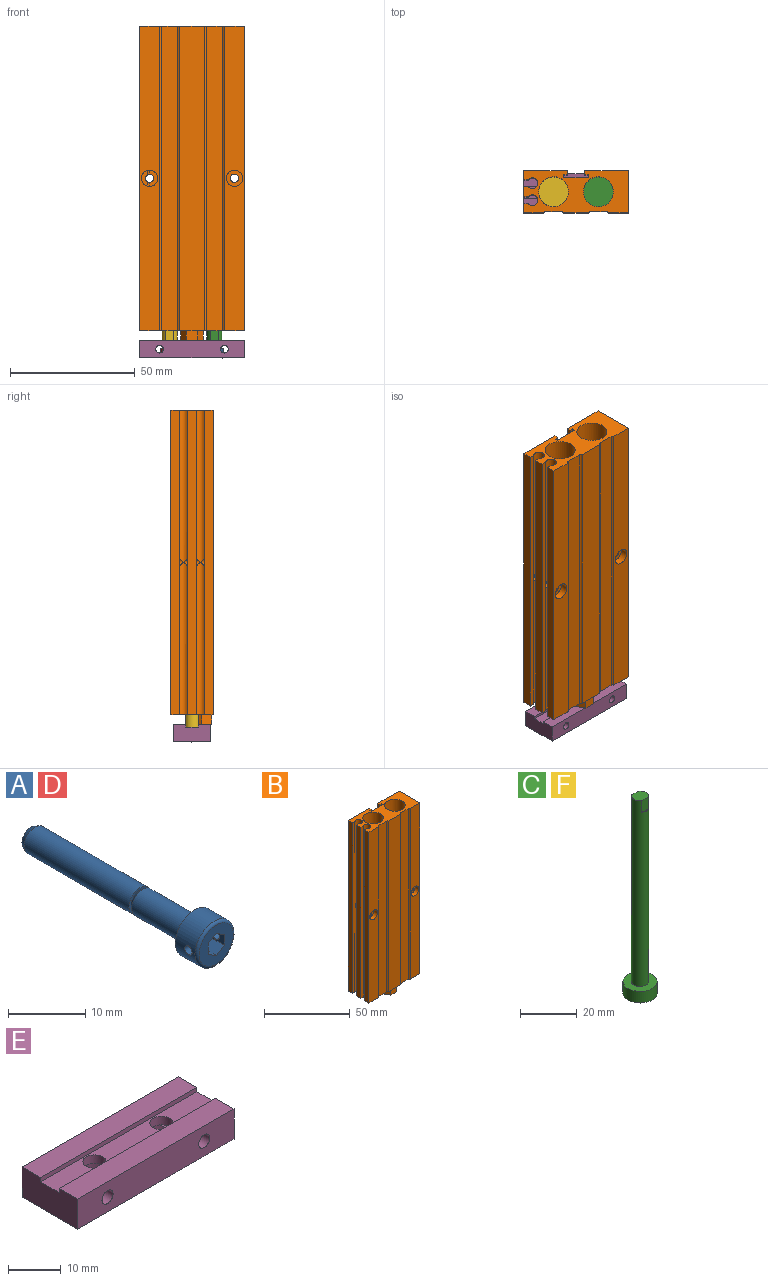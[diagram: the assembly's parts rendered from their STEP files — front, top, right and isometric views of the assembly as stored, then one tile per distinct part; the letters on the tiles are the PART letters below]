
ASSEMBLY  parts=6 mates=11
PART A: 19 faces, bbox 7.6x34x7.6 mm
  f0: cylinder r=3.5mm len=7mm, axis (0,1,0), area 76.8mm2, adj f1,f7,f8,f18
  f1: torus R=3.1mm, axis (0,1,0), area 13.2mm2, adj f0,f17
  f2: cone r=1.81mm half-angle=26.6deg, axis (0,-1,0), area 9.6mm2, adj f3,f16
  f3: cylinder r=2mm len=19.24mm, axis (0,1,0), area 241.8mm2, adj f2,f15
  f4: cone r=1.81mm half-angle=37.2deg, axis (0,-1,0), area 7.1mm2, adj f5,f15
  f5: cylinder r=2mm len=9.5mm, axis (0,1,0), area 119.4mm2, adj f4,f18
  f6: cone r=1.15mm half-angle=60deg, axis (0,-1,0), area 9mm2, adj f9,f10,f11,f12,f13,f14
  f7: cylinder r=0.68mm len=2mm, axis (-1,0,0), area 8.4mm2, adj f0,f9
  f8: cylinder r=0.68mm len=2mm, axis (1,0,0), area 8.4mm2, adj f0,f12
  f9: plane 2.52x1.86mm, normal (1,0,0), area 2.7mm2, adj f6,f7,f10,f14,f17
  f10: plane 2.52x1.63mm, normal (0.5,0,0.87), area 4.2mm2, adj f6,f9,f11,f17
  f11: plane 2.52x1.63mm, normal (-0.5,0,0.87), area 4.2mm2, adj f6,f10,f12,f17
  f12: plane 2.52x1.86mm, normal (-1,0,0), area 2.7mm2, adj f6,f8,f11,f13,f17
  f13: plane 2.52x1.63mm, normal (-0.5,0,-0.87), area 4.2mm2, adj f6,f12,f14,f17
  f14: plane 2.52x1.63mm, normal (0.5,0,-0.87), area 4.2mm2, adj f6,f9,f13,f17
  f15: plane 4x4mm, normal (0,-1,0), area 4.3mm2, adj f3,f4
  f16: plane 3.24x3.24mm, normal (0,1,0), area 8.3mm2, adj f2
  f17: plane 6.2x6.2mm, normal (0,-1,0), area 22.4mm2, adj f1,f9,f10,f11,f12,f13,f14
  f18: plane 7x7mm, normal (0,1,0), area 25.9mm2, adj f0,f5
PART B: 53 faces, bbox 42x17x126 mm
  f0: cylinder r=2.15mm len=122mm, axis (0,0,1), area 1219.4mm2, adj f6,f7,f15,f16,f37,f39,f40,f41
  f1: cylinder r=2.15mm len=122mm, axis (0,0,1), area 1222.4mm2, adj f6,f7,f17,f18,f37,f38
  f2: plane 122x17mm, normal (1,0,0), area 2012.3mm2, adj f6,f7,f11,f13,f32,f33
  f3: cylinder r=6mm len=126mm, axis (0,0,1), area 4544.2mm2, adj f6,f7,f32,f33,f44,f51,f52
  f4: plane 122x7.99mm, normal (0,-1,0), area 941.1mm2, adj f6,f7,f12,f30,f43
  f5: plane 122x9.97mm, normal (0,-1,0), area 1216.5mm2, adj f6,f7,f26,f31
  f6: plane 42x17mm, normal (0,0,1), area 414.9mm2, adj f0,f1,f2,f3,f4,f5,f8,f9
  f7: plane 42x17mm, normal (0,0,-1), area 362.5mm2, adj f0,f1,f2,f3,f4,f5,f8,f9
  f8: plane 122x17.5mm, normal (0,1,0), area 2126.4mm2, adj f6,f7,f9,f21,f38
  f9: plane 122x3.6mm, normal (-1,0,0), area 439.2mm2, adj f6,f7,f8,f17
  f10: plane 122x3.8mm, normal (-1,0,0), area 463.6mm2, adj f6,f7,f16,f18
  f11: plane 122x17.5mm, normal (0,1,0), area 2126.4mm2, adj f2,f6,f7,f20,f34
  f12: plane 122x3.6mm, normal (-1,0,0), area 439.2mm2, adj f4,f6,f7,f15
  f13: plane 122x7.99mm, normal (0,-1,0), area 941.1mm2, adj f2,f6,f7,f27,f36
  f14: cylinder r=6mm len=126mm, axis (0,0,1), area 4608.3mm2, adj f6,f7,f48,f49,f52
  f15: plane 122x1.96mm, normal (0,1,0), area 239.1mm2, adj f0,f6,f7,f12
  f16: plane 122x1.96mm, normal (0,-1,0), area 239.1mm2, adj f0,f6,f7,f10
  f17: plane 122x1.96mm, normal (0,-1,0), area 239.1mm2, adj f1,f6,f7,f9
  f18: plane 122x1.96mm, normal (0,1,0), area 239.1mm2, adj f1,f6,f7,f10
  f19: plane 122x1.5mm, normal (0,-1,0), area 183mm2, adj f6,f7,f20,f25
  f20: plane 122x1.62mm, normal (-1,0,0), area 197.6mm2, adj f6,f7,f11,f19
  f21: plane 122x1.62mm, normal (1,0,0), area 197.6mm2, adj f6,f7,f8,f22
  f22: plane 122x1.5mm, normal (0,-1,0), area 183mm2, adj f6,f7,f21,f23
  f23: plane 122x1.28mm, normal (1,0,0), area 156.2mm2, adj f6,f7,f22,f24
  f24: plane 122x10mm, normal (0,1,0), area 1220mm2, adj f6,f7,f23,f25
  f25: plane 122x1.28mm, normal (-1,0,0), area 156.2mm2, adj f6,f7,f19,f24
  f26: cylinder r=1mm len=122mm, axis (0,0,1), area 154.5mm2, adj f5,f6,f7,f28
  f27: cylinder r=1mm len=122mm, axis (0,0,1), area 154.5mm2, adj f6,f7,f13,f28
  f28: plane 122x6.12mm, normal (0,-1,0), area 746.7mm2, adj f6,f7,f26,f27
  f29: plane 122x6.12mm, normal (0,-1,0), area 746.7mm2, adj f6,f7,f30,f31
  f30: cylinder r=1mm len=122mm, axis (0,0,1), area 154.5mm2, adj f4,f6,f7,f29
  f31: cylinder r=1mm len=122mm, axis (0,0,1), area 154.5mm2, adj f5,f6,f7,f29
  f32: cylinder r=3.13mm len=6.88mm, axis (1,0,0), area 126.7mm2, adj f2,f3
  f33: cylinder r=3.13mm len=6.88mm, axis (1,0,0), area 126.7mm2, adj f2,f3
  f34: cylinder r=1.65mm len=14mm, axis (0,-1,0), area 145.1mm2, adj f11,f35
  f35: plane 6.5x6.5mm, normal (0,-1,0), area 24.6mm2, adj f34,f36
  f36: cylinder r=3.25mm len=6.5mm, axis (0,-1,0), area 61.3mm2, adj f13,f35
  f37: cylinder r=1.65mm len=6.45mm, axis (0,-1,0), area 36.5mm2, adj f0,f1
  f38: cylinder r=1.65mm len=4.93mm, axis (0,-1,0), area 35.9mm2, adj f1,f8
  f39: plane 6.5x3.28mm, normal (0,-1,0), area 12.4mm2, adj f0,f40,f43
  f40: cylinder r=1.65mm len=3.3mm, axis (0,-1,0), area 4.3mm2, adj f0,f39
  f41: cylinder r=1.65mm len=2.69mm, axis (0,-1,0), area 0.5mm2, adj f0,f42
  f42: plane 6.21x2.3mm, normal (0,-1,0), area 9.2mm2, adj f0,f41,f43
  f43: cylinder r=3.25mm len=6.5mm, axis (0,-1,0), area 61.3mm2, adj f0,f4,f39,f42
  f44: plane 4x0.08mm, normal (0.87,0.5,0), area 0.4mm2, adj f3,f7,f45,f52
  f45: plane 4x3.9mm, normal (0.87,-0.5,0), area 18mm2, adj f7,f44,f46,f52
  f46: plane 4.5x4mm, normal (0,-1,0), area 18mm2, adj f7,f45,f47,f52
  f47: plane 4x3.9mm, normal (-0.87,-0.5,0), area 18mm2, adj f7,f46,f48,f52
  f48: plane 4x0.08mm, normal (-0.87,0.5,0), area 0.4mm2, adj f7,f14,f47,f52
  f49: plane 4x1.88mm, normal (-0.87,0.5,0), area 8.7mm2, adj f7,f14,f50,f52
  f50: plane 4.5x4mm, normal (0,1,0), area 18mm2, adj f7,f49,f51,f52
  f51: plane 4x1.88mm, normal (0.87,0.5,0), area 8.7mm2, adj f3,f7,f50,f52
  f52: plane 9.01x7.8mm, normal (0,0,-1), area 52.4mm2, adj f3,f14,f44,f45,f46,f47,f48,f49
PART C: 9 faces, bbox 12x12x85 mm
  f0: cylinder r=3mm len=80mm, axis (0,0,-1), area 1472.8mm2, adj f1,f4,f5,f6,f7,f8
  f1: plane 6x5mm, normal (0,0,1), area 26mm2, adj f0,f5,f8
  f2: cylinder r=6mm len=12mm, axis (0,0,1), area 188.5mm2, adj f3,f4
  f3: plane 12x12mm, normal (0,0,-1), area 113.1mm2, adj f2
  f4: plane 12x12mm, normal (0,0,1), area 84.8mm2, adj f0,f2
  f5: plane 5x3.32mm, normal (0,-1,0), area 16.6mm2, adj f0,f1,f6
  f6: plane 3.32x0.5mm, normal (0,0,1), area 1.1mm2, adj f0,f5
  f7: plane 3.32x0.5mm, normal (0,0,1), area 1.1mm2, adj f0,f8
  f8: plane 5x3.32mm, normal (0,1,0), area 16.6mm2, adj f0,f1,f7
PART D: same geometry as A
PART E: 18 faces, bbox 42x15x7 mm
  f0: plane 42x5mm, normal (0,0,1), area 210mm2, adj f1,f2,f4,f8
  f1: plane 15x7mm, normal (-1,0,0), area 100mm2, adj f0,f3,f4,f5,f6,f7,f8,f9
  f2: plane 15x7mm, normal (1,0,0), area 100mm2, adj f0,f3,f4,f5,f6,f7,f8,f9
  f3: plane 42x7mm, normal (0,1,0), area 279.9mm2, adj f1,f2,f5,f6,f16,f17
  f4: plane 42x7mm, normal (0,-1,0), area 279.9mm2, adj f0,f1,f2,f6,f16,f17
  f5: plane 42x5mm, normal (0,0,1), area 210mm2, adj f1,f2,f3,f7
  f6: plane 42x15mm, normal (0,0,-1), area 523.1mm2, adj f1,f2,f3,f4,f12,f15
  f7: plane 42x1mm, normal (0,-1,0), area 42mm2, adj f1,f2,f5,f9
  f8: plane 42x1mm, normal (0,1,0), area 42mm2, adj f0,f1,f2,f9
  f9: plane 42x5mm, normal (0,0,1), area 179.6mm2, adj f1,f2,f7,f8,f10,f13
  f10: cylinder r=2.2mm len=4.4mm, axis (0,0,-1), area 27.6mm2, adj f9,f11
  f11: plane 8.25x6.71mm, normal (0,0,-1), area 31.4mm2, adj f10,f12,f17
  f12: cylinder r=4.12mm len=8.25mm, axis (0,0,-1), area 89.9mm2, adj f6,f11,f17
  f13: cylinder r=2.2mm len=4.4mm, axis (0,0,-1), area 27.6mm2, adj f9,f14
  f14: plane 8.25x6.71mm, normal (0,0,-1), area 31.4mm2, adj f13,f15,f16
  f15: cylinder r=4.12mm len=8.25mm, axis (0,0,-1), area 89.9mm2, adj f6,f14,f16
  f16: cylinder r=1.5mm len=15mm, axis (0,1,0), area 125.3mm2, adj f3,f4,f14,f15
  f17: cylinder r=1.5mm len=15mm, axis (0,1,0), area 125.3mm2, adj f3,f4,f11,f12
PART F: same geometry as C
PLACE A rot(axis=(1,0,0),90deg) t=(49.66,20.38,-86.13)mm
PLACE B t=(40.66,20.38,-18.13)mm fixed
PLACE C rot(axis=(1,0,0),180deg) t=(49.66,20.38,-44.13)mm
PLACE D rot(axis=(1,0,0),90deg) t=(31.66,20.38,-86.13)mm
PLACE E t=(40.66,20.38,-86.63)mm
PLACE F rot(axis=(1,0,0),180deg) t=(31.66,20.38,-44.13)mm
MATE planar E.f1 <-> B.f9  axis (-1,0,0) through (19.66,20.38,-86.78)mm
MATE slider A.f1 <-> E.f10  axis (0,0,1) through (49.66,20.38,-89.73)mm
MATE planar C.f0 <-> F.f0  axis (0,0,-1) through (49.66,20.38,-84.13)mm
MATE planar E.f9 <-> C.f0  axis (0,0,1) through (40.66,20.38,-84.13)mm
MATE planar D.f17 <-> E.f6  axis (0,0,-1) through (33.16,19.51,-90.13)mm
MATE planar A.f0 <-> E.f11  axis (0,0,1) through (49.66,20.38,-86.13)mm
MATE planar F.f8 <-> E.f8  axis (0,-1,0) through (31.66,17.88,-81.63)mm
MATE slider F.f0 <-> B.f14  axis (0,0,-1) through (31.66,20.38,-4.13)mm
MATE slider E.f13 <-> D.f3  axis (0,0,-1) through (31.66,20.38,-90.13)mm
MATE parallel F.f0 <-> E.f9  axis (0,0,-1) through (31.66,20.38,-84.13)mm
MATE slider B.f3 <-> C.f0  axis (0,0,1) through (49.66,20.38,42.87)mm
